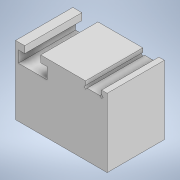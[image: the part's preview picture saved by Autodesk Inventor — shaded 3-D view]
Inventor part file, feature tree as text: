
AUTODESK INVENTOR PART (.ipt)
format: ipt  version: 2021 (Build 250183000, 183)  size: 129,024 bytes
history: native  units: mm
features: extrude x3, sketch x3
ambient origin geometry x8: Origin, YZ Plane, XZ Plane, XY Plane, X Axis, Y Axis, Z Axis, Center Point
bodies: Solid1 (feature_tree)
feature tree (6):
  extrude  "Extrusion1"  Depth=60.0mm
  extrude  "Extrusion2"  Depth=14.0mm
  extrude  "Extrusion3"  Depth=10.0mm
  sketch  "Sketch1"  dims[d0=80.0mm d1=60.0mm]
  sketch  "Sketch2"  dims[d2=50.0mm d3=0.0mm d4=14.0mm]
  sketch  "Sketch5"  dims[d5=9.0mm d6=10.0mm d7=12.5mm d8=25.0mm d9=7.0mm d10=50.0mm d11=0.0mm d27=7.0mm d28=2.0mm d29=2.0mm d30=135.0deg d31=90.0deg d32=5.0mm d33=2.0mm d34=50.0mm d35=0.0mm]
